# Revit family: EKF_EE_НижняяСальниковаяПанельГлухаяTrivia_AVERES
name_source: partatom
category: Электрооборудование
units: mm (PartAtom-declared; Revit-internal decimal feet)

## family parameters
Всегда вертикально = Нет
На основе рабочей плоскости = Да
Общий = Да
При загрузке вырезать с полостями = Нет
Размер круглого соединителя = Использовать диаметр
Тип детали = Силовой щит
Точка расчета площади = Нет

## types (12) — shared parameters
ADSK_Единица измерения = шт.
ADSK_Завод-изготовитель = EKF
ADSK_Количество = 1
ADSK_Марка = Нижняя сальниковая панель глухая
ADSK_Материал = RAL 7035_Сталь
ADSK_Обозначение = Нижняя сальниковая панель глухая
ADSK_Размер_Высота = 20 мм
Изготовитель = EKF
Отметка по умолчанию = 1219.2 мм
Серия номенклатуры = Averes
Степень защиты IP = -
ТВ = EKF_2_TRIVIA_AVERES
Тип установки = -
zero-valued in all types: ADSK_Масса

## per-type parameters (varying)
| type | ADSK_Код изделия | ADSK_Размер_Глубина | ADSK_Размер_Ширина | Тип |
| Нижняя сальниковая панель глухая Ш300 Г400 EKF AVERES | PB3D400 | 323 мм | 223 мм | 457 мм |
| Нижняя сальниковая панель глухая Ш300 Г600 EKF AVERES | PB3D600 | 523 мм | 223 мм | 458 мм |
| Нижняя сальниковая панель глухая Ш300 Г800 EKF AVERES | PB3D800 | 723 мм | 223 мм | 459 мм |
| Нижняя сальниковая панель глухая Ш400 Г400 EKF AVERES | PB4D400 | 323 мм | 323 мм | 460 мм |
| Нижняя сальниковая панель глухая Ш400 Г600 EKF AVERES | PB4D600 | 523 мм | 323 мм | 461 мм |
| Нижняя сальниковая панель глухая Ш400 Г800 EKF AVERES | PB4D800 | 723 мм | 323 мм | 462 мм |
| Нижняя сальниковая панель глухая Ш600 Г400 EKF AVERES | PB6D400 | 323 мм | 523 мм | 463 мм |
| Нижняя сальниковая панель глухая Ш600 Г600 EKF AVERES | PB6D600 | 523 мм | 523 мм | 464 мм |
| Нижняя сальниковая панель глухая Ш600 Г800 EKF AVERES | PB6D800 | 723 мм | 523 мм | 465 мм |
| Нижняя сальниковая панель глухая Ш800 Г400 EKF AVERES | PB8D400 | 323 мм | 723 мм | 466 мм |
| Нижняя сальниковая панель глухая Ш800 Г600 EKF AVERES | PB8D600 | 523 мм | 723 мм | 467 мм |
| Нижняя сальниковая панель глухая Ш800 Г800 EKF AVERES | PB8D800 | 723 мм | 723 мм | 468 мм |

note: column(s) folded — value = type name in every type: ADSK_Наименование
